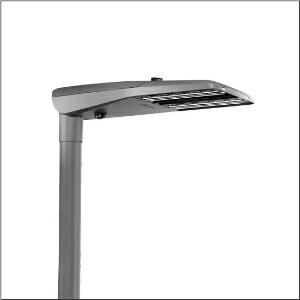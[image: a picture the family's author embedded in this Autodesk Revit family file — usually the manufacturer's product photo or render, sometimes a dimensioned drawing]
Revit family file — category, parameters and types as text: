
# Revit family: streetlight_sl_11_iq_midi___st1_2a_5xc3a21y08me_d9a7
name_source: partatom
category: Lighting Fixtures
units: mm (PartAtom-declared; Revit-internal decimal feet)

## family parameters
Cut with Voids When Loaded = No
Host = Face
Light Source = No
Part Type = Normal
Room Calculation Point = No
Round Connector Dimension = Use Diameter
Shared = No

## types (1)
- --- (1 x LED, 14840 lm, 122.8 W, 2200K)
    Apparent Load = 123 VA
    CIE Flux Codes = 32 70 96 100 100
    Color Rendering = 70
    Color Temperature = 2200K
    Default Elevation = 1800 mm
    Description = Streetlight SL 11 iQ midi, mast luminaire, primary light control with 3 zone facetted reflector, of plastic, silver coated, highly specular, primary optical cover: cover, of PMMA, transparent, light distribution: ST1.2a, light emission: direct distribution, primary light characteristic: asymmetric, installation type: post-top, side-entry, LED, High Power LED, rated luminous flux: 14.840lm, luminous efficacy: 121lm/W, light colour: 722, colour temperature: 2200K, control: presetting dimming logarithmic, Street-Remote, Auto-Match, Temp-Guard, Lumen-Switch, Night-Set, Smart-Wire, Light-Fading, Desk-Remote (wireless, voltage-free reading and setting of iQ features in the workshop via application-optimized NFC function/RFID function), optimised constant luminous flux control (CLO 2.0), with cable H07RN-F 5x 1.5mm², mains connection: 230..240V, AC, 50/60Hz, connection cable pre-assembled, cable length: 12,5m, start of lifetime: 123W, end of service life: 130W, reduction: 56W, luminaire housing, of diecast aluminium, powder-coated, Siteco® metallic grey (DB 702S), please order mast flange separately, inclination adjustable without tools: 0°, 5°, 10°, 15° (post-top) | 0°, -5°, -10°, -15° (side-entry), sealing non-destructively replaceable, multi-level sealing system, length: 780mm, width: 376mm, height: 118mm, mast flange for spigot size: 42mm (side-entry): 5XC10008XM4, 60/48mm (side-entry/post-top): 5XC10108XM2, 76/60mm (side-entry/post-top): 5XC10108XM1, equipment: Power, Smart Interface below and above, protection rating (complete): IP66, insulation class (complete): insulation class II (safety insulation), certification: CE, ENEC, VDE, UKCA, impact resistance: IK09, permissible operating ambient temperature for outdoor applications: -25..+50°C, standard-compliant lighting for roads and squares, Environmental Product Declaration (EPD) tested and certified by an independent institute, packaging unit: 1 piece

Light Distribution: ST1.2a
    Height = 118 mm
    Lamp = 1 x LED
    Lamp Light Flux = 14840 lm
    Lamp Power = 122.8 W
    Lamp count = 1
    Length = 780 mm
    Luminous efficacy = 121 lm/W
    Manufacturer = Siteco
    ModVariant = No
    Model = 5XC3A21Y08ME
    Number of Poles = 1
    OnlyDefault = Yes
    Power Factor = 1
    Product Name = Streetlight SL 11 iQ midi | ST1.2a
    Product group = mast luminaire | pylon top
    ProductGroupID = 6100
    Protection Class = Protection class II
    Protection Degree = IP 66
    RLX_Detail_Level = 1
    RLX_Emergency_Light_Flux = 0 lm
    RLX_Emergency_Type = 0
    RLX_Emergency_Type_DB = No
    RlxData = <blob elided: 69629 chars, md5=8dee3ada>
    Socket = socket
    Standby Power = 0 W
    System Light Flux = 14840 lm
    System Power = 123 W
    Type Comments = factory setting: luminous flux: 100 % | dim-lin: 254 | 553 mA
    Type Image = l_1004429.jpg
    URL = http://relux.com
    VarID = @adj_061039
    Voltage = 0 V
    Weight = 0.00 kg
    Width = 376 mm

## geometry (parser evidence)
native form markers: Blend x4, Sweep x9
no freeform markers — native parametric forms only
